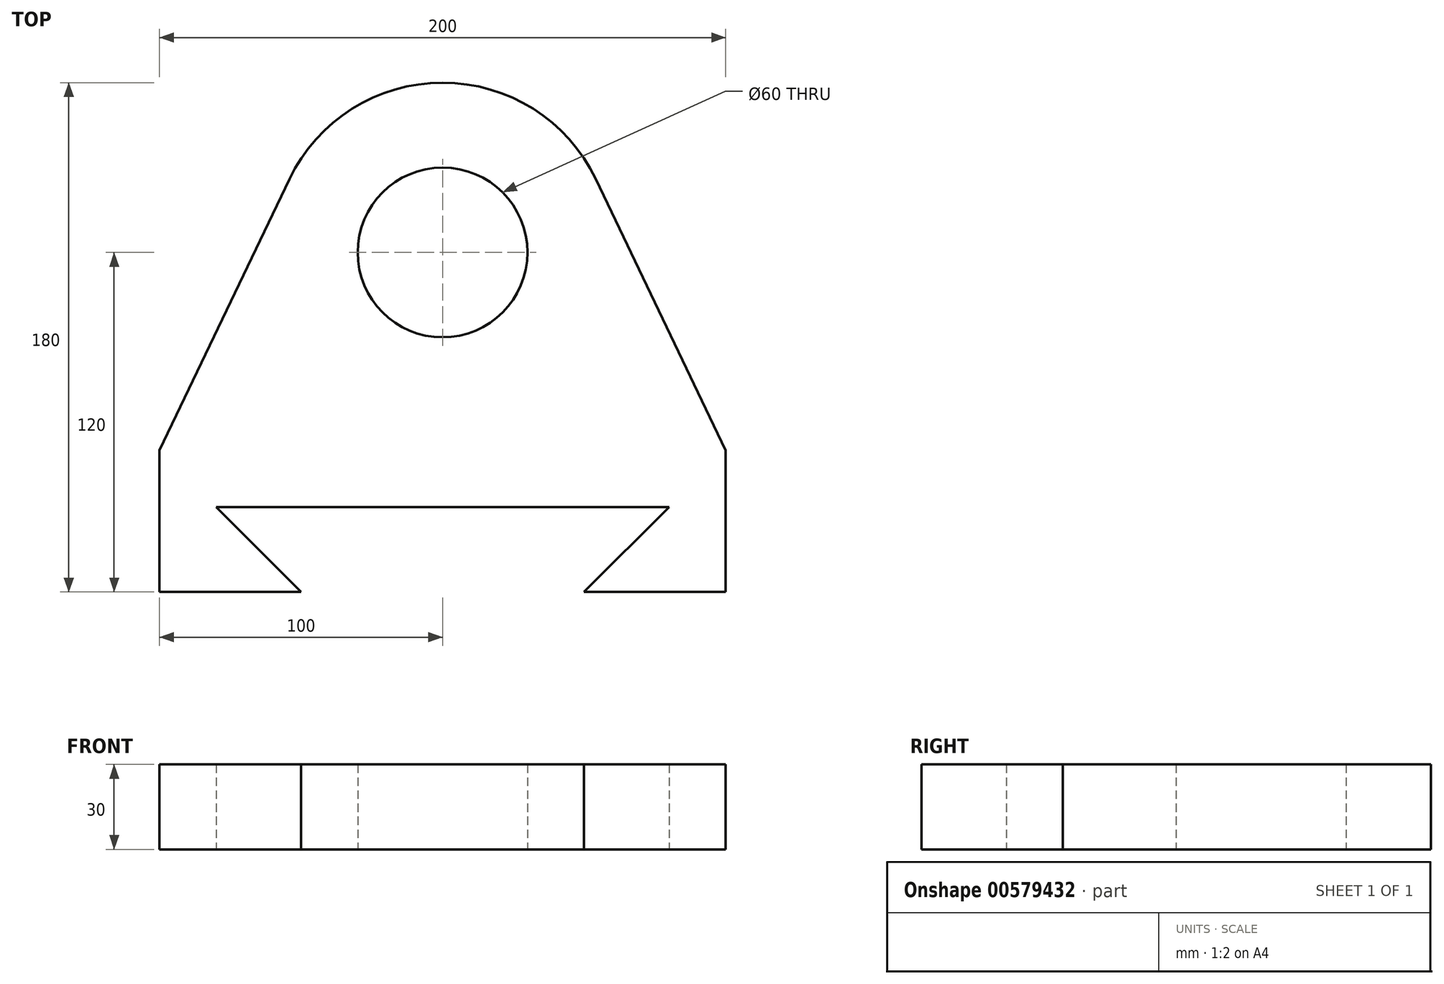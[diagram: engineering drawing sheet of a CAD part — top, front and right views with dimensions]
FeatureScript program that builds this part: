
annotation { "Feature Type Name" : "Feature", "Feature Type Description" : "" }
export const myFeature = defineFeature(function(context is Context, id is Id, definition is map)
    precondition{}
    {
        {
            var Q0;
            Q0=qCreatedBy(makeId("Top.planeOp"),FACE);
            var sketch = newSketch(context, id + "F0", { "sketchPlane" : qUnion([Q0])});
            skCircle(sketch, "E0", {"center": v(0, 0) * mm, "radius": 30 * mm});
            skCircle(sketch, "E1", {"center": v(0, 0) * mm, "radius": 60 * mm});
            skLineSegment(sketch, "E2", {"start": v(-100, -70) * mm, "end": v(100, -70) * mm});
            skLineSegment(sketch, "E3", {"start": v(54.13, 25.9) * mm, "end": v(100, -70) * mm});
            skLineSegment(sketch, "E4", {"start": v(-100, -70) * mm, "end": v(-54.13, 25.9) * mm});
            skLineSegment(sketch, "E5", {"start": v(0, 0) * mm, "end": v(0, -70) * mm});
            skLineSegment(sketch, "E6", {"start": v(-100, -70) * mm, "end": v(-100, -120) * mm});
            skLineSegment(sketch, "E7", {"start": v(100, -70) * mm, "end": v(100, -120) * mm});
            skLineSegment(sketch, "E8", {"start": v(-100, -120) * mm, "end": v(-50, -120) * mm});
            skLineSegment(sketch, "E9", {"start": v(-50, -120) * mm, "end": v(-80, -90) * mm});
            skLineSegment(sketch, "E10", {"start": v(50, -120) * mm, "end": v(80, -90) * mm});
            skLineSegment(sketch, "E11", {"start": v(-80, -90) * mm, "end": v(80, -90) * mm});
            skLineSegment(sketch, "E12.trimOffspring", {"start": v(50, -120) * mm, "end": v(100, -120) * mm});
            skSolve(sketch);
        }
        {
            var Q0;
            Q0 = qSketchRegion(id + "F0", true);
            extrude(context, id + "F1", {"entities" : qUnion([Q0]), "depth" : 30 * mm, "offsetDistance" : 25 * mm});
        }
    });
